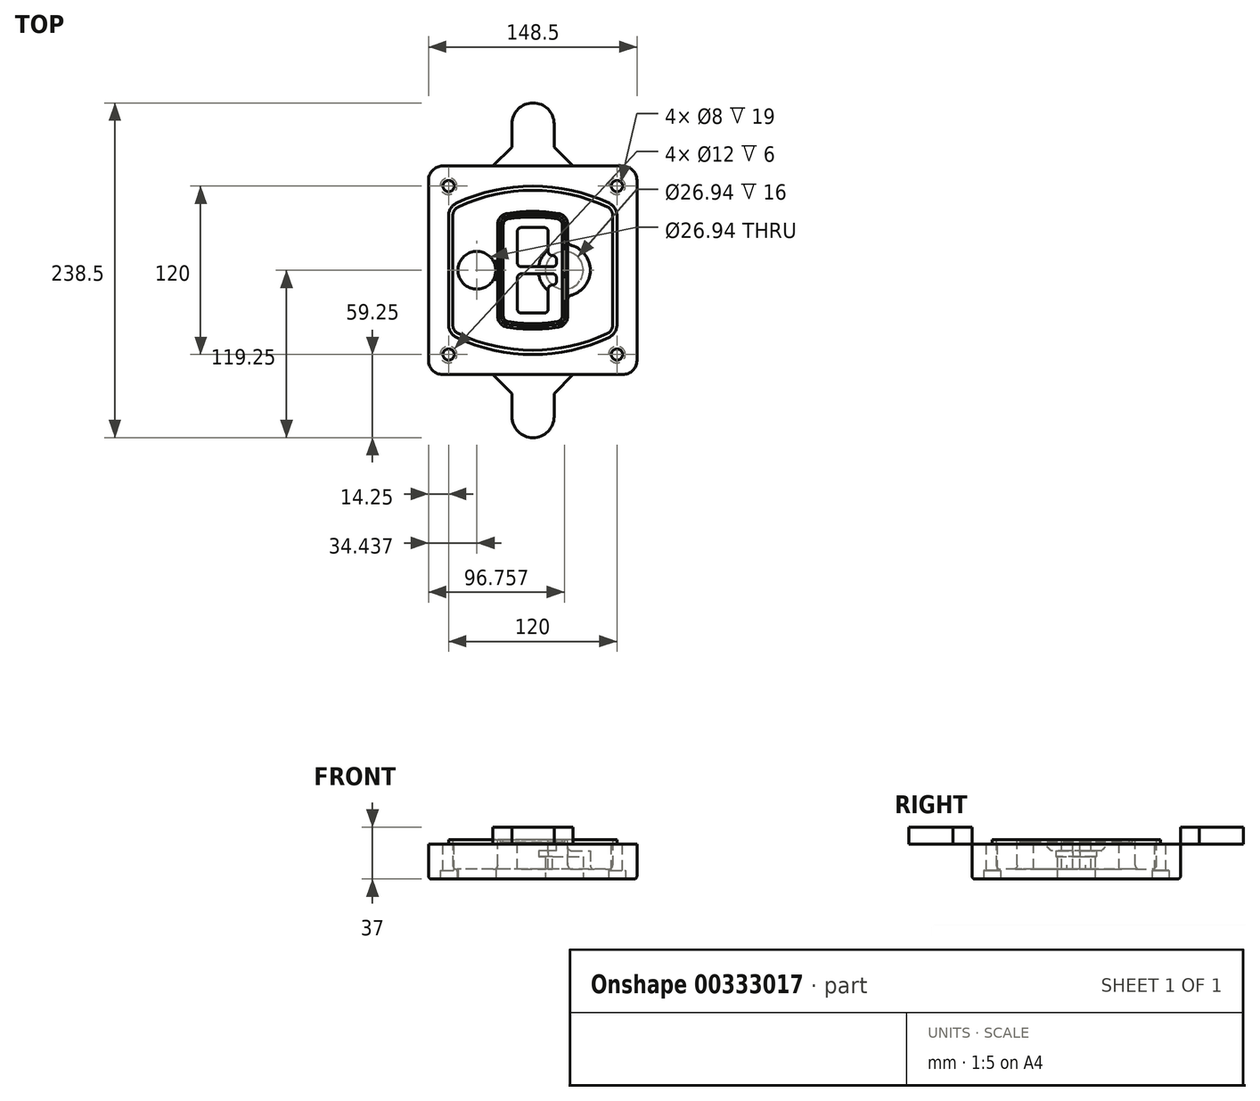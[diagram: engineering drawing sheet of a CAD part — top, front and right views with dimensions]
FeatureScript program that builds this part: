
annotation { "Feature Type Name" : "Feature", "Feature Type Description" : "" }
export const myFeature = defineFeature(function(context is Context, id is Id, definition is map)
    precondition{}
    {
        {
            var Q0;
            Q0=qCreatedBy(makeId("Top.planeOp"),FACE);
            var sketch = newSketch(context, id + "F0", { "sketchPlane" : qUnion([Q0])});
            skPoint(sketch, "E0.rect.middle", {"position": v(0, 0) * mm});
            skLineSegment(sketch, "E1.bottom", {"start": v(-64.25, -74.25) * mm, "end": v(64.25, -74.25) * mm});
            skLineSegment(sketch, "E1.top", {"start": v(-64.25, 74.25) * mm, "end": v(64.25, 74.25) * mm});
            skLineSegment(sketch, "E1.left", {"start": v(-74.25, -64.25) * mm, "end": v(-74.25, 64.25) * mm});
            skLineSegment(sketch, "E1.right", {"start": v(74.25, -64.25) * mm, "end": v(74.25, 64.25) * mm});
            skLineSegment(sketch, "E2", {"start": v(-74.25, 74.25) * mm, "end": v(74.25, -74.25) * mm, "construction": true});
            skLineSegment(sketch, "E3", {"start": v(74.25, 74.25) * mm, "end": v(-74.25, -74.25) * mm, "construction": true});
            skCircle(sketch, "E4", {"center": v(-60, 60) * mm, "radius": 4 * mm});
            skCircle(sketch, "E5", {"center": v(60, 60) * mm, "radius": 4 * mm});
            skCircle(sketch, "E6", {"center": v(60, -60) * mm, "radius": 4 * mm});
            skCircle(sketch, "E7", {"center": v(-60, -60) * mm, "radius": 4 * mm});
            skLineSegment(sketch, "E8", {"start": v(-60, 60) * mm, "end": v(60, 60) * mm, "construction": true});
            skLineSegment(sketch, "E9", {"start": v(60, 60) * mm, "end": v(60, -60) * mm, "construction": true});
            skLineSegment(sketch, "E10", {"start": v(60, -60) * mm, "end": v(-60, -60) * mm, "construction": true});
            skLineSegment(sketch, "E11", {"start": v(-60, -60) * mm, "end": v(-60, 60) * mm, "construction": true});
            skLineSegment(sketch, "E12", {"start": v(-60, 38.83) * mm, "end": v(-60, -38.83) * mm});
            skLineSegment(sketch, "E13", {"start": v(60, 38.83) * mm, "end": v(60, -38.83) * mm});
            skArc(sketch, "E14", {"start": v(54.26, 47.88) * mm, "mid": v(0, 60) * mm, "end": v(-54.26, 47.88) * mm});
            skArc(sketch, "E15", {"start": v(-54.26, -47.88) * mm, "mid": v(0, -60) * mm, "end": v(54.26, -47.88) * mm});
            skLineSegment(sketch, "E16", {"start": v(-60, 0) * mm, "end": v(60, 0) * mm, "construction": true});
            skPoint(sketch, "E17.visualSharp", {"position": v(-60, -45) * mm});
            skArc(sketch, "E17.filletArc", {"start": v(-60, -38.83) * mm, "mid": v(-58.44, -44.2) * mm, "end": v(-54.26, -47.88) * mm});
            skPoint(sketch, "E18.visualSharp", {"position": v(-60, 45) * mm});
            skArc(sketch, "E18.filletArc", {"start": v(-54.26, 47.88) * mm, "mid": v(-58.44, 44.2) * mm, "end": v(-60, 38.83) * mm});
            skPoint(sketch, "E19.visualSharp", {"position": v(60, 45) * mm});
            skArc(sketch, "E19.filletArc", {"start": v(60, 38.83) * mm, "mid": v(58.44, 44.2) * mm, "end": v(54.26, 47.88) * mm});
            skPoint(sketch, "E20.visualSharp", {"position": v(60, -45) * mm});
            skArc(sketch, "E20.filletArc", {"start": v(54.26, -47.88) * mm, "mid": v(58.44, -44.2) * mm, "end": v(60, -38.83) * mm});
            skPoint(sketch, "E21.visualSharp", {"position": v(-74.25, 74.25) * mm});
            skArc(sketch, "E21.filletArc", {"start": v(-64.25, 74.25) * mm, "mid": v(-71.32, 71.32) * mm, "end": v(-74.25, 64.25) * mm});
            skPoint(sketch, "E22.visualSharp", {"position": v(74.25, 74.25) * mm});
            skArc(sketch, "E22.filletArc", {"start": v(74.25, 64.25) * mm, "mid": v(71.32, 71.32) * mm, "end": v(64.25, 74.25) * mm});
            skPoint(sketch, "E23.visualSharp", {"position": v(74.25, -74.25) * mm});
            skArc(sketch, "E23.filletArc", {"start": v(64.25, -74.25) * mm, "mid": v(71.32, -71.32) * mm, "end": v(74.25, -64.25) * mm});
            skPoint(sketch, "E24.visualSharp", {"position": v(-74.25, -74.25) * mm});
            skArc(sketch, "E24.filletArc", {"start": v(-74.25, -64.25) * mm, "mid": v(-71.32, -71.32) * mm, "end": v(-64.25, -74.25) * mm});
            skArc(sketch, "E25.0", {"start": v(57, 38.83) * mm, "mid": v(55.9, 42.58) * mm, "end": v(52.98, 45.17) * mm});
            skLineSegment(sketch, "E25.1", {"start": v(57, 38.83) * mm, "end": v(57, -38.83) * mm});
            skArc(sketch, "E25.2", {"start": v(52.98, -45.17) * mm, "mid": v(55.9, -42.58) * mm, "end": v(57, -38.83) * mm});
            skArc(sketch, "E25.3", {"start": v(-52.98, -45.17) * mm, "mid": v(0, -57) * mm, "end": v(52.98, -45.17) * mm});
            skArc(sketch, "E25.4", {"start": v(-57, -38.83) * mm, "mid": v(-55.9, -42.58) * mm, "end": v(-52.98, -45.17) * mm});
            skArc(sketch, "E25.5", {"start": v(52.98, 45.17) * mm, "mid": v(0, 57) * mm, "end": v(-52.98, 45.17) * mm});
            skLineSegment(sketch, "E25.6", {"start": v(-57, 38.83) * mm, "end": v(-57, -38.83) * mm});
            skArc(sketch, "E25.7", {"start": v(-52.98, 45.17) * mm, "mid": v(-55.9, 42.58) * mm, "end": v(-57, 38.83) * mm});
            skArc(sketch, "E26.0", {"start": v(-55.96, 51.5) * mm, "mid": v(-61.82, 46.33) * mm, "end": v(-64, 38.83) * mm});
            skArc(sketch, "E26.1", {"start": v(55.96, 51.5) * mm, "mid": v(0, 64) * mm, "end": v(-55.96, 51.5) * mm});
            skArc(sketch, "E26.2", {"start": v(64, 38.83) * mm, "mid": v(61.82, 46.33) * mm, "end": v(55.96, 51.5) * mm});
            skLineSegment(sketch, "E26.3", {"start": v(64, 38.83) * mm, "end": v(64, -38.83) * mm});
            skArc(sketch, "E26.4", {"start": v(55.96, -51.5) * mm, "mid": v(61.82, -46.33) * mm, "end": v(64, -38.83) * mm});
            skLineSegment(sketch, "E26.5", {"start": v(-64, 38.83) * mm, "end": v(-64, -38.83) * mm});
            skArc(sketch, "E26.6", {"start": v(-55.96, -51.5) * mm, "mid": v(0, -64) * mm, "end": v(55.96, -51.5) * mm});
            skArc(sketch, "E26.7", {"start": v(-64, -38.83) * mm, "mid": v(-61.82, -46.33) * mm, "end": v(-55.96, -51.5) * mm});
            skSolve(sketch);
        }
        {
            var Q0;
            Q0=makeQuery(id+"F0.imprint","IMPRINT",FACE,{"disambiguationData":[TD([[makeQuery(id+"F0.imprint","IMPRINT",EDGE,{"derivedFrom":sQuery(id+"F0.wireOp",EDGE,"E1.bottom")}),1.0]])]});
            var Q1;
            Q1=makeQuery(id+"F0.imprint","IMPRINT",FACE,{"disambiguationData":[TD([[makeQuery(id+"F0.imprint","IMPRINT",EDGE,{"derivedFrom":sQuery(id+"F0.wireOp",EDGE,"E12")}),1.0]])]});
            var Q2;
            Q2=makeQuery(id+"F0.imprint","IMPRINT",FACE,{"disambiguationData":[TD([[makeQuery(id+"F0.imprint","IMPRINT",EDGE,{"derivedFrom":sQuery(id+"F0.wireOp",EDGE,"E25.0")}),1.0]])]});
            var Q3;
            Q3=makeQuery(id+"F0.imprint","IMPRINT",FACE,{"disambiguationData":[TD([[makeQuery(id+"F0.imprint","IMPRINT",EDGE,{"derivedFrom":sQuery(id+"F0.wireOp",EDGE,"E12")}),-1.0]])]});
            extrude(context, id + "F1", {"entities" : qUnion([Q0, Q1, Q2, Q3]), "oppositeDirection" : true, "depth" : 25 * mm});
        }
        {
            var Q0;
            Q0=makeQuery(id+"F0.imprint","IMPRINT",FACE,{"disambiguationData":[TD([[makeQuery(id+"F0.imprint","IMPRINT",EDGE,{"derivedFrom":sQuery(id+"F0.wireOp",EDGE,"E12")}),1.0]])]});
            extrude(context, id + "F2", {"entities" : qUnion([Q0]), "operationType" : NewBodyOperationType.ADD, "depth" : 3 * mm});
        }
        {
            var Q0;
            Q0=makeQuery(id+"F0.imprint","IMPRINT",FACE,{"disambiguationData":[TD([[makeQuery(id+"F0.imprint","IMPRINT",EDGE,{"derivedFrom":sQuery(id+"F0.wireOp",EDGE,"E25.0")}),1.0]])]});
            extrude(context, id + "F3", {"entities" : qUnion([Q0]), "operationType" : NewBodyOperationType.REMOVE, "oppositeDirection" : true, "depth" : 18 * mm});
        }
        {
            var Q0;
            Q0=makeQuery(id+"F2.opExtrude","CAP_FACE",FACE,{"disambiguationData":[OSD([sQuery(id+"F0.wireOp",EDGE,"E12"),sQuery(id+"F0.wireOp",EDGE,"E13"),sQuery(id+"F0.wireOp",EDGE,"E14"),sQuery(id+"F0.wireOp",EDGE,"E15"),sQuery(id+"F0.wireOp",EDGE,"E17.filletArc"),sQuery(id+"F0.wireOp",EDGE,"E18.filletArc"),sQuery(id+"F0.wireOp",EDGE,"E19.filletArc"),sQuery(id+"F0.wireOp",EDGE,"E20.filletArc"),sQuery(id+"F0.wireOp",EDGE,"E25.0"),sQuery(id+"F0.wireOp",EDGE,"E25.1"),sQuery(id+"F0.wireOp",EDGE,"E25.2"),sQuery(id+"F0.wireOp",EDGE,"E25.3"),sQuery(id+"F0.wireOp",EDGE,"E25.4"),sQuery(id+"F0.wireOp",EDGE,"E25.5"),sQuery(id+"F0.wireOp",EDGE,"E25.6"),sQuery(id+"F0.wireOp",EDGE,"E25.7")])],"isStart":false});
            var sketch = newSketch(context, id + "F4", { "sketchPlane" : qUnion([Q0])});
            skArc(sketch, "E27.0", {"start": v(-18.34, -40.45) * mm, "mid": v(0, -42) * mm, "end": v(18.34, -40.45) * mm});
            skArc(sketch, "E28.0", {"start": v(18.34, 40.45) * mm, "mid": v(0, 42) * mm, "end": v(-18.34, 40.45) * mm});
            skLineSegment(sketch, "E29", {"start": v(-25, 32.57) * mm, "end": v(-25, -32.57) * mm});
            skLineSegment(sketch, "E30", {"start": v(25, 32.57) * mm, "end": v(25, -32.57) * mm});
            skLineSegment(sketch, "E31", {"start": v(-25, 39.1) * mm, "end": v(25, 39.1) * mm, "construction": true});
            skLineSegment(sketch, "E32", {"start": v(-25, -39.1) * mm, "end": v(25, -39.1) * mm, "construction": true});
            skPoint(sketch, "E33.visualSharp", {"position": v(-25, 39.1) * mm});
            skArc(sketch, "E33.filletArc", {"start": v(-18.34, 40.45) * mm, "mid": v(-23.11, 37.73) * mm, "end": v(-25, 32.57) * mm});
            skPoint(sketch, "E34.visualSharp", {"position": v(25, 39.1) * mm});
            skArc(sketch, "E34.filletArc", {"start": v(25, 32.57) * mm, "mid": v(23.11, 37.73) * mm, "end": v(18.34, 40.45) * mm});
            skPoint(sketch, "E35.visualSharp", {"position": v(25, -39.1) * mm});
            skArc(sketch, "E35.filletArc", {"start": v(18.34, -40.45) * mm, "mid": v(23.11, -37.73) * mm, "end": v(25, -32.57) * mm});
            skPoint(sketch, "E36.visualSharp", {"position": v(-25, -39.1) * mm});
            skArc(sketch, "E36.filletArc", {"start": v(-25, -32.57) * mm, "mid": v(-23.11, -37.73) * mm, "end": v(-18.34, -40.45) * mm});
            skArc(sketch, "E37.0", {"start": v(52.98, 45.17) * mm, "mid": v(0, 57) * mm, "end": v(-52.98, 45.17) * mm});
            skArc(sketch, "E37.1", {"start": v(-52.98, 45.17) * mm, "mid": v(-55.9, 42.58) * mm, "end": v(-57, 38.83) * mm});
            skLineSegment(sketch, "E37.2", {"start": v(-57, 38.83) * mm, "end": v(-57, -38.83) * mm});
            skArc(sketch, "E37.3", {"start": v(-57, -38.83) * mm, "mid": v(-55.9, -42.58) * mm, "end": v(-52.98, -45.17) * mm});
            skArc(sketch, "E37.4", {"start": v(-52.98, -45.17) * mm, "mid": v(0, -57) * mm, "end": v(52.98, -45.17) * mm});
            skArc(sketch, "E37.5", {"start": v(52.98, -45.17) * mm, "mid": v(55.9, -42.58) * mm, "end": v(57, -38.83) * mm});
            skLineSegment(sketch, "E37.6", {"start": v(57, 38.83) * mm, "end": v(57, -38.83) * mm});
            skArc(sketch, "E37.7", {"start": v(57, 38.83) * mm, "mid": v(55.9, 42.58) * mm, "end": v(52.98, 45.17) * mm});
            skLineSegment(sketch, "E38.0", {"start": v(23, 32.57) * mm, "end": v(23, -32.57) * mm});
            skArc(sketch, "E38.1", {"start": v(18, -38.48) * mm, "mid": v(21.58, -36.44) * mm, "end": v(23, -32.57) * mm});
            skArc(sketch, "E38.2", {"start": v(-18, -38.48) * mm, "mid": v(0, -40) * mm, "end": v(18, -38.48) * mm});
            skArc(sketch, "E38.3", {"start": v(-23, -32.57) * mm, "mid": v(-21.58, -36.44) * mm, "end": v(-18, -38.48) * mm});
            skLineSegment(sketch, "E38.4", {"start": v(-23, 32.57) * mm, "end": v(-23, -32.57) * mm});
            skArc(sketch, "E38.5", {"start": v(23, 32.57) * mm, "mid": v(21.58, 36.44) * mm, "end": v(18, 38.48) * mm});
            skArc(sketch, "E38.6", {"start": v(-18, 38.48) * mm, "mid": v(-21.58, 36.44) * mm, "end": v(-23, 32.57) * mm});
            skArc(sketch, "E38.7", {"start": v(18, 38.48) * mm, "mid": v(0, 40) * mm, "end": v(-18, 38.48) * mm});
            skArc(sketch, "E39.0", {"start": v(21, 32.57) * mm, "mid": v(20.06, 35.15) * mm, "end": v(17.67, 36.5) * mm});
            skLineSegment(sketch, "E39.1", {"start": v(21, 32.57) * mm, "end": v(21, -32.57) * mm});
            skArc(sketch, "E39.2", {"start": v(17.67, -36.5) * mm, "mid": v(20.06, -35.15) * mm, "end": v(21, -32.57) * mm});
            skArc(sketch, "E39.3", {"start": v(-17.67, -36.5) * mm, "mid": v(0, -38) * mm, "end": v(17.67, -36.5) * mm});
            skArc(sketch, "E39.4", {"start": v(-21, -32.57) * mm, "mid": v(-20.06, -35.15) * mm, "end": v(-17.67, -36.5) * mm});
            skArc(sketch, "E39.5", {"start": v(17.67, 36.5) * mm, "mid": v(0, 38) * mm, "end": v(-17.67, 36.5) * mm});
            skLineSegment(sketch, "E39.6", {"start": v(-21, 32.57) * mm, "end": v(-21, -32.57) * mm});
            skArc(sketch, "E39.7", {"start": v(-17.67, 36.5) * mm, "mid": v(-20.06, 35.15) * mm, "end": v(-21, 32.57) * mm});
            skLineSegment(sketch, "E40", {"start": v(-25, 0) * mm, "end": v(25, 0) * mm, "construction": true});
            skLineSegment(sketch, "E41", {"start": v(-11, 5.5) * mm, "end": v(-11, 27.5) * mm});
            skLineSegment(sketch, "E42", {"start": v(-8, 30.5) * mm, "end": v(8, 30.5) * mm});
            skLineSegment(sketch, "E43", {"start": v(11, 27.5) * mm, "end": v(11, 13.5) * mm});
            skLineSegment(sketch, "E44", {"start": v(14, 10.5) * mm, "end": v(14, 10.5) * mm});
            skLineSegment(sketch, "E45", {"start": v(17, 7.5) * mm, "end": v(17, 5.5) * mm});
            skLineSegment(sketch, "E46", {"start": v(14, 2.5) * mm, "end": v(-8, 2.5) * mm});
            skPoint(sketch, "E47.visualSharp", {"position": v(-11, 30.5) * mm});
            skArc(sketch, "E47.filletArc", {"start": v(-8, 30.5) * mm, "mid": v(-10.12, 29.62) * mm, "end": v(-11, 27.5) * mm});
            skPoint(sketch, "E48.visualSharp", {"position": v(11, 30.5) * mm});
            skArc(sketch, "E48.filletArc", {"start": v(11, 27.5) * mm, "mid": v(10.12, 29.62) * mm, "end": v(8, 30.5) * mm});
            skPoint(sketch, "E49.visualSharp", {"position": v(11, 10.5) * mm});
            skArc(sketch, "E49.filletArc", {"start": v(11, 13.5) * mm, "mid": v(11.88, 11.38) * mm, "end": v(14, 10.5) * mm});
            skPoint(sketch, "E50.visualSharp", {"position": v(17, 10.5) * mm});
            skArc(sketch, "E50.filletArc", {"start": v(17, 7.5) * mm, "mid": v(16.12, 9.62) * mm, "end": v(14, 10.5) * mm});
            skPoint(sketch, "E51.visualSharp", {"position": v(17, 2.5) * mm});
            skArc(sketch, "E51.filletArc", {"start": v(14, 2.5) * mm, "mid": v(16.12, 3.38) * mm, "end": v(17, 5.5) * mm});
            skPoint(sketch, "E52.visualSharp", {"position": v(-11, 2.5) * mm});
            skArc(sketch, "E52.filletArc", {"start": v(-11, 5.5) * mm, "mid": v(-10.12, 3.38) * mm, "end": v(-8, 2.5) * mm});
            skLineSegment(sketch, "E53.0.MirrorCS", {"start": v(14, -2.5) * mm, "end": v(-8, -2.5) * mm});
            skArc(sketch, "E54.0.MirrorCS", {"start": v(-11, -5.5) * mm, "mid": v(-10.12, -3.38) * mm, "end": v(-8, -2.5) * mm});
            skLineSegment(sketch, "E55.0.MirrorCS", {"start": v(-11, -5.5) * mm, "end": v(-11, -27.5) * mm});
            skArc(sketch, "E56.0.MirrorCS", {"start": v(-8, -30.5) * mm, "mid": v(-10.12, -29.62) * mm, "end": v(-11, -27.5) * mm});
            skLineSegment(sketch, "E57.0.MirrorCS", {"start": v(-8, -30.5) * mm, "end": v(8, -30.5) * mm});
            skArc(sketch, "E58.0.MirrorCS", {"start": v(11, -27.5) * mm, "mid": v(10.12, -29.62) * mm, "end": v(8, -30.5) * mm});
            skLineSegment(sketch, "E59.0.MirrorCS", {"start": v(11, -27.5) * mm, "end": v(11, -13.5) * mm});
            skArc(sketch, "E60.0.MirrorCS", {"start": v(11, -13.5) * mm, "mid": v(11.88, -11.38) * mm, "end": v(14, -10.5) * mm});
            skArc(sketch, "E61.0.MirrorCS", {"start": v(17, -7.5) * mm, "mid": v(16.12, -9.62) * mm, "end": v(14, -10.5) * mm});
            skLineSegment(sketch, "E62.0.MirrorCS", {"start": v(17, -7.5) * mm, "end": v(17, -5.5) * mm});
            skArc(sketch, "E63.0.MirrorCS", {"start": v(14, -2.5) * mm, "mid": v(16.12, -3.38) * mm, "end": v(17, -5.5) * mm});
            skSolve(sketch);
        }
        {
            var Q0;
            Q0=makeQuery(id+"F4.imprint","IMPRINT",FACE,{"disambiguationData":[TD([[makeQuery(id+"F4.imprint","IMPRINT",EDGE,{"derivedFrom":sQuery(id+"F4.wireOp",EDGE,"E27.0")}),1.0]])]});
            var Q1;
            Q1=makeQuery(id+"F4.imprint","IMPRINT",FACE,{"disambiguationData":[TD([[makeQuery(id+"F4.imprint","IMPRINT",EDGE,{"derivedFrom":sQuery(id+"F4.wireOp",EDGE,"E38.0")}),-1.0]])]});
            var Q2;
            Q2=makeQuery(id+"F4.imprint","IMPRINT",FACE,{"disambiguationData":[TD([[makeQuery(id+"F4.imprint","IMPRINT",EDGE,{"derivedFrom":sQuery(id+"F4.wireOp",EDGE,"E39.0")}),1.0]])]});
            extrude(context, id + "F5", {"entities" : qUnion([Q0, Q1, Q2]), "operationType" : NewBodyOperationType.ADD, "endBound" : BoundingType.UP_TO_NEXT, "oppositeDirection" : true, "depth" : 25 * mm});
        }
        {
            var Q0;
            Q0=makeQuery(id+"F4.imprint","IMPRINT",FACE,{"disambiguationData":[TD([[makeQuery(id+"F4.imprint","IMPRINT",EDGE,{"derivedFrom":sQuery(id+"F4.wireOp",EDGE,"E38.0")}),-1.0]])]});
            extrude(context, id + "F6", {"entities" : qUnion([Q0]), "operationType" : NewBodyOperationType.REMOVE, "oppositeDirection" : true, "depth" : 2 * mm});
        }
        {
            var Q0;
            Q0=makeQuery(id+"F1.opExtrude","CAP_FACE",FACE,{"disambiguationData":[OSD([sQuery(id+"F0.wireOp",EDGE,"E1.bottom"),sQuery(id+"F0.wireOp",EDGE,"E1.top"),sQuery(id+"F0.wireOp",EDGE,"E1.left"),sQuery(id+"F0.wireOp",EDGE,"E1.right"),sQuery(id+"F0.wireOp",EDGE,"E4"),sQuery(id+"F0.wireOp",EDGE,"E5"),sQuery(id+"F0.wireOp",EDGE,"E6"),sQuery(id+"F0.wireOp",EDGE,"E7"),sQuery(id+"F0.wireOp",EDGE,"E21.filletArc"),sQuery(id+"F0.wireOp",EDGE,"E22.filletArc"),sQuery(id+"F0.wireOp",EDGE,"E23.filletArc"),sQuery(id+"F0.wireOp",EDGE,"E24.filletArc")])],"isStart":false});
            var sketch = newSketch(context, id + "F7", { "sketchPlane" : qUnion([Q0])});
            skCircle(sketch, "E64", {"center": v(22.5, 0) * mm, "radius": 13.47 * mm});
            skCircle(sketch, "E65", {"center": v(-39.81, 0) * mm, "radius": 13.47 * mm});
            skLineSegment(sketch, "E66", {"start": v(74.25, 0) * mm, "end": v(-74.25, 0) * mm});
            skCircle(sketch, "E67", {"center": v(22.5, 0) * mm, "radius": 18.47 * mm});
            skCircle(sketch, "E68", {"center": v(60, -60) * mm, "radius": 6 * mm});
            skCircle(sketch, "E69", {"center": v(-60, -60) * mm, "radius": 6 * mm});
            skCircle(sketch, "E70", {"center": v(-60, 60) * mm, "radius": 6 * mm});
            skCircle(sketch, "E71", {"center": v(60, 60) * mm, "radius": 6 * mm});
            skSolve(sketch);
        }
        {
            var Q0;
            {var subQ1=sQuery(id+"F7.wireOp",EDGE,"E66");var subQ4=sQuery(id+"F7.wireOp",EDGE,"E64");var subQ6=makeQuery(id+"F7.imprint","INTERSECT",VERTEX,{"disambiguationData":[OD(0.0)],"derivedFrom":[subQ4,subQ1]});Q0=makeQuery(id+"F7.imprint","IMPRINT",FACE,{"disambiguationData":[TD([[makeQuery(id+"F7.imprint","IMPRINT",EDGE,{"disambiguationData":[TD([[subQ6,-1.0]])],"derivedFrom":subQ4}),-1.0]])]});}
            var Q1;
            {var subQ0=sQuery(id+"F7.wireOp",EDGE,"E66");var subQ1=sQuery(id+"F7.wireOp",EDGE,"E64");var subQ3=makeQuery(id+"F7.imprint","INTERSECT",VERTEX,{"disambiguationData":[OD(0.0)],"derivedFrom":[subQ1,subQ0]});Q1=makeQuery(id+"F7.imprint","IMPRINT",FACE,{"disambiguationData":[TD([[makeQuery(id+"F7.imprint","IMPRINT",EDGE,{"disambiguationData":[TD([[subQ3,-1.0]])],"derivedFrom":subQ1}),1.0]])]});}
            var Q2;
            {var subQ0=sQuery(id+"F7.wireOp",EDGE,"E66");var subQ1=sQuery(id+"F7.wireOp",EDGE,"E64");var subQ3=makeQuery(id+"F7.imprint","INTERSECT",VERTEX,{"disambiguationData":[OD(0.0)],"derivedFrom":[subQ1,subQ0]});Q2=makeQuery(id+"F7.imprint","IMPRINT",FACE,{"disambiguationData":[TD([[makeQuery(id+"F7.imprint","IMPRINT",EDGE,{"disambiguationData":[TD([[subQ3,1.0]])],"derivedFrom":subQ1}),1.0]])]});}
            var Q3;
            {var subQ1=sQuery(id+"F7.wireOp",EDGE,"E66");var subQ4=sQuery(id+"F7.wireOp",EDGE,"E64");var subQ6=makeQuery(id+"F7.imprint","INTERSECT",VERTEX,{"disambiguationData":[OD(0.0)],"derivedFrom":[subQ4,subQ1]});Q3=makeQuery(id+"F7.imprint","IMPRINT",FACE,{"disambiguationData":[TD([[makeQuery(id+"F7.imprint","IMPRINT",EDGE,{"disambiguationData":[TD([[subQ6,1.0]])],"derivedFrom":subQ4}),-1.0]])]});}
            extrude(context, id + "F8", {"entities" : qUnion([Q0, Q1, Q2, Q3]), "operationType" : NewBodyOperationType.ADD, "oppositeDirection" : true, "depth" : 20 * mm});
        }
        {
            var Q0;
            {var subQ0=sQuery(id+"F7.wireOp",EDGE,"E66");var subQ1=sQuery(id+"F7.wireOp",EDGE,"E64");var subQ3=makeQuery(id+"F7.imprint","INTERSECT",VERTEX,{"disambiguationData":[OD(0.0)],"derivedFrom":[subQ1,subQ0]});Q0=makeQuery(id+"F7.imprint","IMPRINT",FACE,{"disambiguationData":[TD([[makeQuery(id+"F7.imprint","IMPRINT",EDGE,{"disambiguationData":[TD([[subQ3,-1.0]])],"derivedFrom":subQ1}),1.0]])]});}
            var Q1;
            {var subQ0=sQuery(id+"F7.wireOp",EDGE,"E66");var subQ1=sQuery(id+"F7.wireOp",EDGE,"E64");var subQ3=makeQuery(id+"F7.imprint","INTERSECT",VERTEX,{"disambiguationData":[OD(0.0)],"derivedFrom":[subQ1,subQ0]});Q1=makeQuery(id+"F7.imprint","IMPRINT",FACE,{"disambiguationData":[TD([[makeQuery(id+"F7.imprint","IMPRINT",EDGE,{"disambiguationData":[TD([[subQ3,1.0]])],"derivedFrom":subQ1}),1.0]])]});}
            extrude(context, id + "F9", {"entities" : qUnion([Q0, Q1]), "operationType" : NewBodyOperationType.REMOVE, "oppositeDirection" : true, "depth" : 16 * mm});
        }
        {
            var Q0;
            {var subQ0=sQuery(id+"F7.wireOp",EDGE,"E66");var subQ1=sQuery(id+"F7.wireOp",EDGE,"E65");var subQ3=makeQuery(id+"F7.imprint","INTERSECT",VERTEX,{"disambiguationData":[OD(0.0)],"derivedFrom":[subQ1,subQ0]});Q0=makeQuery(id+"F7.imprint","IMPRINT",FACE,{"disambiguationData":[TD([[makeQuery(id+"F7.imprint","IMPRINT",EDGE,{"disambiguationData":[TD([[subQ3,-1.0]])],"derivedFrom":subQ1}),1.0]])]});}
            var Q1;
            {var subQ0=sQuery(id+"F7.wireOp",EDGE,"E66");var subQ1=sQuery(id+"F7.wireOp",EDGE,"E65");var subQ3=makeQuery(id+"F7.imprint","INTERSECT",VERTEX,{"disambiguationData":[OD(0.0)],"derivedFrom":[subQ1,subQ0]});Q1=makeQuery(id+"F7.imprint","IMPRINT",FACE,{"disambiguationData":[TD([[makeQuery(id+"F7.imprint","IMPRINT",EDGE,{"disambiguationData":[TD([[subQ3,1.0]])],"derivedFrom":subQ1}),1.0]])]});}
            extrude(context, id + "F10", {"entities" : qUnion([Q0, Q1]), "operationType" : NewBodyOperationType.REMOVE, "oppositeDirection" : true, "depth" : 25 * mm});
        }
        {
            var Q0;
            Q0=makeQuery(id+"F7.imprint","IMPRINT",FACE,{"disambiguationData":[TD([[makeQuery(id+"F7.imprint","IMPRINT",EDGE,{"derivedFrom":sQuery(id+"F7.wireOp",EDGE,"E68")}),1.0]])]});
            var Q1;
            Q1=makeQuery(id+"F7.imprint","IMPRINT",FACE,{"disambiguationData":[TD([[makeQuery(id+"F7.imprint","IMPRINT",EDGE,{"derivedFrom":makeQuery(id+"F1.opExtrude","CAP_EDGE",EDGE,{"disambiguationData":[OSD([sQuery(id+"F0.wireOp",EDGE,"E5")])],"isStart":false})}),-1.0]])]});
            var Q2;
            Q2=makeQuery(id+"F7.imprint","IMPRINT",FACE,{"disambiguationData":[TD([[makeQuery(id+"F7.imprint","IMPRINT",EDGE,{"derivedFrom":sQuery(id+"F7.wireOp",EDGE,"E69")}),1.0]])]});
            var Q3;
            Q3=makeQuery(id+"F7.imprint","IMPRINT",FACE,{"disambiguationData":[TD([[makeQuery(id+"F7.imprint","IMPRINT",EDGE,{"derivedFrom":makeQuery(id+"F1.opExtrude","CAP_EDGE",EDGE,{"disambiguationData":[OSD([sQuery(id+"F0.wireOp",EDGE,"E4")])],"isStart":false})}),-1.0]])]});
            var Q4;
            Q4=makeQuery(id+"F7.imprint","IMPRINT",FACE,{"disambiguationData":[TD([[makeQuery(id+"F7.imprint","IMPRINT",EDGE,{"derivedFrom":sQuery(id+"F7.wireOp",EDGE,"E70")}),1.0]])]});
            var Q5;
            Q5=makeQuery(id+"F7.imprint","IMPRINT",FACE,{"disambiguationData":[TD([[makeQuery(id+"F7.imprint","IMPRINT",EDGE,{"derivedFrom":makeQuery(id+"F1.opExtrude","CAP_EDGE",EDGE,{"disambiguationData":[OSD([sQuery(id+"F0.wireOp",EDGE,"E7")])],"isStart":false})}),-1.0]])]});
            var Q6;
            Q6=makeQuery(id+"F7.imprint","IMPRINT",FACE,{"disambiguationData":[TD([[makeQuery(id+"F7.imprint","IMPRINT",EDGE,{"derivedFrom":sQuery(id+"F7.wireOp",EDGE,"E71")}),1.0]])]});
            var Q7;
            Q7=makeQuery(id+"F7.imprint","IMPRINT",FACE,{"disambiguationData":[TD([[makeQuery(id+"F7.imprint","IMPRINT",EDGE,{"derivedFrom":makeQuery(id+"F1.opExtrude","CAP_EDGE",EDGE,{"disambiguationData":[OSD([sQuery(id+"F0.wireOp",EDGE,"E6")])],"isStart":false})}),-1.0]])]});
            extrude(context, id + "F11", {"entities" : qUnion([Q0, Q1, Q2, Q3, Q4, Q5, Q6, Q7]), "operationType" : NewBodyOperationType.REMOVE, "oppositeDirection" : true, "depth" : 6 * mm});
        }
        {
            var Q0;
            Q0=makeQuery(id+"F9.boolean.opBoolean","COPY",FACE,{"derivedFrom":makeQuery(id+"F9.opExtrude","CAP_FACE",FACE,{"disambiguationData":[OSD([sQuery(id+"F7.wireOp",EDGE,"E64")])],"isStart":false})});
            var sketch = newSketch(context, id + "F12", { "sketchPlane" : qUnion([Q0])});
            skArc(sketch, "E72.0", {"start": v(11, 14.45) * mm, "mid": v(6.45, 9.13) * mm, "end": v(4.2, 2.5) * mm});
            skArc(sketch, "E72.1", {"start": v(4.2, -2.5) * mm, "mid": v(6.45, -9.13) * mm, "end": v(11, -14.45) * mm});
            skLineSegment(sketch, "E73", {"start": v(4.2, -2.5) * mm, "end": v(14, -2.5) * mm});
            skLineSegment(sketch, "E74.0", {"start": v(14, 2.5) * mm, "end": v(4.2, 2.5) * mm});
            skArc(sketch, "E74.1", {"start": v(14, 2.5) * mm, "mid": v(16.12, 3.38) * mm, "end": v(17, 5.5) * mm});
            skLineSegment(sketch, "E74.2", {"start": v(17, 7.5) * mm, "end": v(17, 5.5) * mm});
            skArc(sketch, "E74.3", {"start": v(17, 7.5) * mm, "mid": v(16.12, 9.62) * mm, "end": v(14, 10.5) * mm});
            skArc(sketch, "E74.4", {"start": v(11, 13.5) * mm, "mid": v(11.88, 11.38) * mm, "end": v(14, 10.5) * mm});
            skLineSegment(sketch, "E74.5", {"start": v(11, 14.45) * mm, "end": v(11, 13.5) * mm});
            skLineSegment(sketch, "E74.7", {"start": v(14, -2.5) * mm, "end": v(4.2, -2.5) * mm});
            skArc(sketch, "E74.8", {"start": v(14, -2.5) * mm, "mid": v(16.12, -3.38) * mm, "end": v(17, -5.5) * mm});
            skLineSegment(sketch, "E74.9", {"start": v(17, -7.5) * mm, "end": v(17, -5.5) * mm});
            skArc(sketch, "E74.10", {"start": v(17, -7.5) * mm, "mid": v(16.12, -9.62) * mm, "end": v(14, -10.5) * mm});
            skArc(sketch, "E74.11", {"start": v(11, -13.5) * mm, "mid": v(11.88, -11.38) * mm, "end": v(14, -10.5) * mm});
            skLineSegment(sketch, "E74.12", {"start": v(11, -14.45) * mm, "end": v(11, -13.5) * mm});
            skPoint(sketch, "E75.orphan", {"position": v(11, -27.5) * mm});
            skPoint(sketch, "E76.orphan", {"position": v(-8, -2.5) * mm});
            skPoint(sketch, "E77.orphan", {"position": v(-8, 2.5) * mm});
            skPoint(sketch, "E78.orphan", {"position": v(11, 27.5) * mm});
            skSolve(sketch);
        }
        {
            var Q0;
            {var subQ7=sQuery(id+"F12.wireOp",EDGE,"E72.0");var subQ14=sQuery(id+"F12.wireOp",EDGE,"E72.1");var subQ16=sQuery(id+"F12.wireOp",EDGE,"E74.1");var subQ18=sQuery(id+"F12.wireOp",EDGE,"E74.8");Q0=qUnion([makeQuery(id+"F12.imprint","IMPRINT",FACE,{"disambiguationData":[TD([[makeQuery(id+"F12.imprint","IMPRINT",EDGE,{"derivedFrom":subQ7}),1.0]])]}),makeQuery(id+"F12.imprint","IMPRINT",FACE,{"disambiguationData":[TD([[makeQuery(id+"F12.imprint","IMPRINT",EDGE,{"derivedFrom":subQ14}),1.0]])]}),makeQuery(id+"F12.imprint","IMPRINT",FACE,{"disambiguationData":[TD([[makeQuery(id+"F12.imprint","IMPRINT",EDGE,{"derivedFrom":subQ16}),1.0]])]}),makeQuery(id+"F12.imprint","IMPRINT",FACE,{"disambiguationData":[TD([[makeQuery(id+"F12.imprint","IMPRINT",EDGE,{"derivedFrom":subQ18}),-1.0]])]})]);}
            var Q1;
            Q1=makeQuery(id+"F5.boolean.opBoolean","SPLIT",FACE,{"disambiguationData":[TD([makeQuery(id+"F5.opExtrude","SWEPT_FACE",FACE,{"disambiguationData":[OSD([sQuery(id+"F4.wireOp",EDGE,"E41")])]})])],"derivedFrom":makeQuery(id+"F3.boolean.opBoolean","COPY",FACE,{"derivedFrom":makeQuery(id+"F3.opExtrude","CAP_FACE",FACE,{"disambiguationData":[OSD([sQuery(id+"F0.wireOp",EDGE,"E25.0"),sQuery(id+"F0.wireOp",EDGE,"E25.1"),sQuery(id+"F0.wireOp",EDGE,"E25.2"),sQuery(id+"F0.wireOp",EDGE,"E25.3"),sQuery(id+"F0.wireOp",EDGE,"E25.4"),sQuery(id+"F0.wireOp",EDGE,"E25.5"),sQuery(id+"F0.wireOp",EDGE,"E25.6"),sQuery(id+"F0.wireOp",EDGE,"E25.7")])],"isStart":false})})});
            extrude(context, id + "F13", {"entities" : qUnion([Q0]), "operationType" : NewBodyOperationType.REMOVE, "endBound" : BoundingType.UP_TO_SURFACE, "endBoundEntityFace" : qUnion([Q1]), "depth" : 25 * mm});
        }
        {
            var Q0;
            Q0=makeQuery(id+"F3.boolean.opBoolean","COPY",EDGE,{"derivedFrom":makeQuery(id+"F3.opExtrude","CAP_EDGE",EDGE,{"disambiguationData":[OSD([sQuery(id+"F0.wireOp",EDGE,"E25.6")])],"isStart":false})});
            var Q1;
            Q1=makeQuery(id+"F8.boolean.opBoolean","INTERSECT",EDGE,{"derivedFrom":[makeQuery(id+"F5.opExtrude","SWEPT_FACE",FACE,{"disambiguationData":[OSD([sQuery(id+"F4.wireOp",EDGE,"E30")])]}),makeQuery(id+"F8.opExtrude","CAP_FACE",FACE,{"disambiguationData":[OSD([sQuery(id+"F7.wireOp",EDGE,"E67")])],"isStart":false})]});
            var Q2;
            Q2=makeQuery(id+"F8.boolean.opBoolean","INTERSECT",EDGE,{"disambiguationData":[OD(1.0)],"derivedFrom":[makeQuery(id+"F5.opExtrude","SWEPT_FACE",FACE,{"disambiguationData":[OSD([sQuery(id+"F4.wireOp",EDGE,"E30")])]}),makeQuery(id+"F8.opExtrude","SWEPT_FACE",FACE,{"disambiguationData":[OSD([sQuery(id+"F7.wireOp",EDGE,"E67")])]})]});
            var Q3;
            {var subQ0=sQuery(id+"F4.wireOp",EDGE,"E30");Q3=makeQuery(id+"F8.boolean.opBoolean","SPLIT",EDGE,{"disambiguationData":[TD([makeQuery(id+"F5.opExtrude","SWEPT_FACE",FACE,{"disambiguationData":[OSD([sQuery(id+"F4.wireOp",EDGE,"E35.filletArc")])]})])],"derivedFrom":makeQuery(id+"F5.opExtrude","CAP_EDGE",EDGE,{"disambiguationData":[OSD([subQ0])],"isStart":false})});}
            var Q4;
            {var subQ0=sQuery(id+"F0.wireOp",EDGE,"E25.7");var subQ1=sQuery(id+"F0.wireOp",EDGE,"E25.1");var subQ2=sQuery(id+"F0.wireOp",EDGE,"E25.6");var subQ3=sQuery(id+"F0.wireOp",EDGE,"E25.5");var subQ4=sQuery(id+"F0.wireOp",EDGE,"E25.4");var subQ5=sQuery(id+"F0.wireOp",EDGE,"E25.0");var subQ6=sQuery(id+"F0.wireOp",EDGE,"E25.2");var subQ7=sQuery(id+"F0.wireOp",EDGE,"E25.3");Q4=makeQuery(id+"F8.boolean.opBoolean","INTERSECT",EDGE,{"derivedFrom":[makeQuery(id+"F5.boolean.opBoolean","SPLIT",FACE,{"disambiguationData":[TD([makeQuery(id+"F2.opExtrude","SWEPT_FACE",FACE,{"disambiguationData":[OSD([subQ5])]})])],"derivedFrom":makeQuery(id+"F3.boolean.opBoolean","COPY",FACE,{"derivedFrom":makeQuery(id+"F3.opExtrude","CAP_FACE",FACE,{"disambiguationData":[OSD([subQ5,subQ1,subQ6,subQ7,subQ4,subQ3,subQ2,subQ0])],"isStart":false})})}),makeQuery(id+"F8.opExtrude","SWEPT_FACE",FACE,{"disambiguationData":[OSD([sQuery(id+"F7.wireOp",EDGE,"E67")])]})]});}
            var Q5;
            Q5=makeQuery(id+"F8.boolean.opBoolean","INTERSECT",EDGE,{"disambiguationData":[OD(0.0)],"derivedFrom":[makeQuery(id+"F5.opExtrude","SWEPT_FACE",FACE,{"disambiguationData":[OSD([sQuery(id+"F4.wireOp",EDGE,"E30")])]}),makeQuery(id+"F8.opExtrude","SWEPT_FACE",FACE,{"disambiguationData":[OSD([sQuery(id+"F7.wireOp",EDGE,"E67")])]})]});
            fillet(context, id + "F14", {"entities" : qUnion([Q0, Q1, Q2, Q3, Q4, Q5]), "radius" : 3 * mm, "tangentPropagation" : true, "allowEdgeOverflow" : false});
        }
        {
            var Q0;
            Q0=makeQuery(id+"F1.opExtrude","CAP_EDGE",EDGE,{"disambiguationData":[OSD([sQuery(id+"F0.wireOp",EDGE,"E1.bottom")])],"isStart":false});
            fillet(context, id + "F15", {"entities" : qUnion([Q0]), "radius" : 2 * mm, "tangentPropagation" : true, "allowEdgeOverflow" : false});
        }
        {
            var Q0;
            {var subQ0=sQuery(id+"F0.wireOp",EDGE,"E21.filletArc");var subQ1=sQuery(id+"F0.wireOp",EDGE,"E7");var subQ2=sQuery(id+"F0.wireOp",EDGE,"E6");var subQ3=sQuery(id+"F0.wireOp",EDGE,"E5");var subQ4=sQuery(id+"F0.wireOp",EDGE,"E4");var subQ5=sQuery(id+"F0.wireOp",EDGE,"E22.filletArc");var subQ6=sQuery(id+"F0.wireOp",EDGE,"E1.bottom");var subQ7=sQuery(id+"F0.wireOp",EDGE,"E1.right");var subQ8=sQuery(id+"F0.wireOp",EDGE,"E1.top");var subQ9=sQuery(id+"F0.wireOp",EDGE,"E1.left");var subQ10=sQuery(id+"F0.wireOp",EDGE,"E23.filletArc");var subQ11=sQuery(id+"F0.wireOp",EDGE,"E24.filletArc");Q0=makeQuery(id+"F2.boolean.opBoolean","SPLIT",FACE,{"disambiguationData":[TD([makeQuery(id+"F1.opExtrude","SWEPT_FACE",FACE,{"disambiguationData":[OSD([subQ6])]})])],"derivedFrom":makeQuery(id+"F1.opExtrude","CAP_FACE",FACE,{"disambiguationData":[OSD([subQ6,subQ8,subQ9,subQ7,subQ4,subQ3,subQ2,subQ1,subQ0,subQ5,subQ10,subQ11])],"isStart":true})});}
            var sketch = newSketch(context, id + "F16", { "sketchPlane" : qUnion([Q0])});
            skLineSegment(sketch, "E79", {"start": v(0, 75.13) * mm, "end": v(0, 104.25) * mm, "construction": true});
            skPoint(sketch, "E79.startSnap0", {"position": v(0, 74.25) * mm});
            skCircle(sketch, "E80", {"center": v(0, 104.25) * mm, "radius": 6 * mm});
            skLineSegment(sketch, "E81", {"start": v(-28.36, 74.25) * mm, "end": v(-14.8, 87.8) * mm});
            skLineSegment(sketch, "E82", {"start": v(-14.8, 87.8) * mm, "end": v(-14.8, 104.25) * mm});
            skLineSegment(sketch, "E83", {"start": v(15.2, 87.8) * mm, "end": v(28.76, 74.25) * mm});
            skLineSegment(sketch, "E84", {"start": v(15.2, 87.8) * mm, "end": v(15.2, 104.25) * mm});
            skArc(sketch, "E85", {"start": v(15.2, 104.25) * mm, "mid": v(0.2, 119.25) * mm, "end": v(-14.8, 104.25) * mm});
            skLineSegment(sketch, "E86", {"start": v(-74.25, 0) * mm, "end": v(72.74, 0) * mm, "construction": true});
            skPoint(sketch, "E86.endSnap0", {"position": v(74.25, 0) * mm});
            skLineSegment(sketch, "E87.MirrorCS", {"start": v(0, -75.13) * mm, "end": v(0, -104.25) * mm, "construction": true});
            skLineSegment(sketch, "E88.MirrorCS", {"start": v(15.2, -87.8) * mm, "end": v(28.76, -74.25) * mm});
            skLineSegment(sketch, "E89.MirrorCS", {"start": v(15.2, -87.8) * mm, "end": v(15.2, -104.25) * mm});
            skArc(sketch, "E90.MirrorCS", {"start": v(15.2, -104.25) * mm, "mid": v(0.2, -119.25) * mm, "end": v(-14.8, -104.25) * mm});
            skLineSegment(sketch, "E91.MirrorCS", {"start": v(-14.8, -87.8) * mm, "end": v(-14.8, -104.25) * mm});
            skLineSegment(sketch, "E92.MirrorCS", {"start": v(-28.36, -74.25) * mm, "end": v(-14.8, -87.8) * mm});
            skCircle(sketch, "E93.MirrorC", {"center": v(0, -104.25) * mm, "radius": 6 * mm});
            skSolve(sketch);
        }
        {
            var Q0;
            Q0 = qSketchRegion(id + "F16", true);
            var Q1;
            {var subQ0=sQuery(id+"F16.wireOp",EDGE,"E88.MirrorCS");Q1=makeQuery(id+"F16.imprint","IMPRINT",FACE,{"disambiguationData":[TD([[makeQuery(id+"F16.imprint","IMPRINT",EDGE,{"derivedFrom":subQ0}),1.0]])]});}
            var Q2;
            Q2=makeQuery(id+"F16.imprint","IMPRINT",FACE,{"disambiguationData":[TD([[makeQuery(id+"F16.imprint","IMPRINT",EDGE,{"derivedFrom":sQuery(id+"F16.wireOp",EDGE,"E80")}),-1.0]])]});
            extrude(context, id + "F17", {"entities" : qUnion([Q0, Q1, Q2]), "depth" : 12 * mm});
        }
    });
